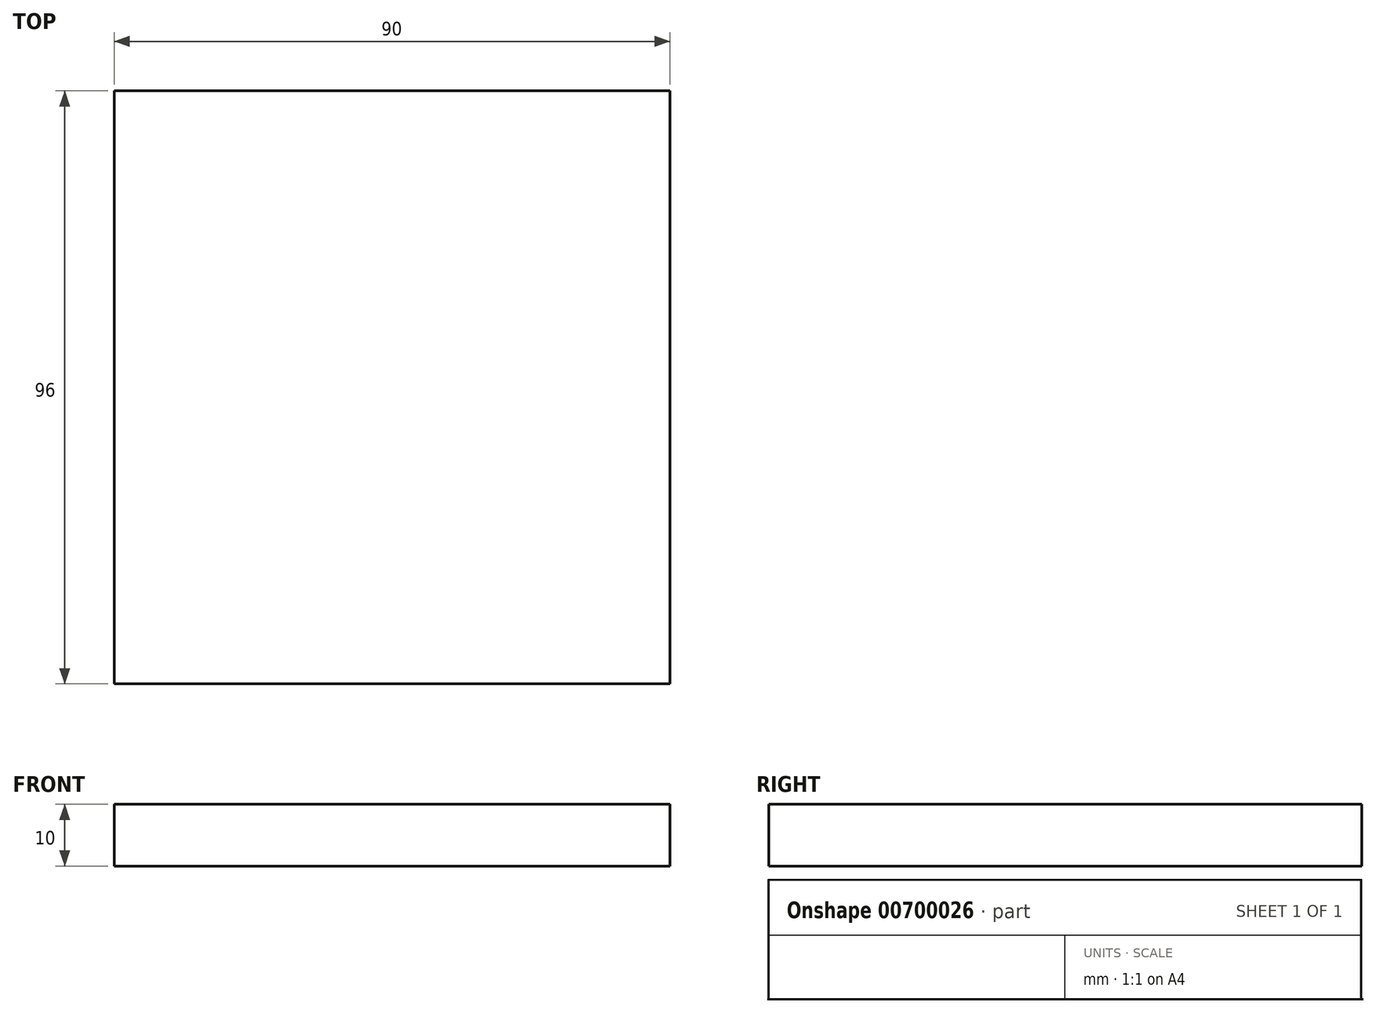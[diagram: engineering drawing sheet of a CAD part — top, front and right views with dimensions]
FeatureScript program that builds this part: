
annotation { "Feature Type Name" : "Feature", "Feature Type Description" : "" }
export const myFeature = defineFeature(function(context is Context, id is Id, definition is map)
    precondition{}
    {
        {
            var Q0;
            Q0=qCreatedBy(makeId("Top.planeOp"),FACE);
            var sketch = newSketch(context, id + "F0", { "sketchPlane" : qUnion([Q0])});
            skLineSegment(sketch, "E0.bottom", {"start": v(45, -46.6) * mm, "end": v(-45, -46.6) * mm});
            skLineSegment(sketch, "E0.top", {"start": v(45, 49.4) * mm, "end": v(-45, 49.4) * mm});
            skLineSegment(sketch, "E0.left", {"start": v(45, -46.6) * mm, "end": v(45, 49.4) * mm});
            skLineSegment(sketch, "E0.right", {"start": v(-45, -46.6) * mm, "end": v(-45, 49.4) * mm});
            skPoint(sketch, "E0.middle", {"position": v(0, 1.4) * mm});
            skSolve(sketch);
        }
        {
            var Q0;
            Q0 = qSketchRegion(id + "F0", true);
            extrude(context, id + "F1", {"entities" : qUnion([Q0]), "depth" : 10 * mm, "offsetDistance" : 25 * mm});
        }
    });
